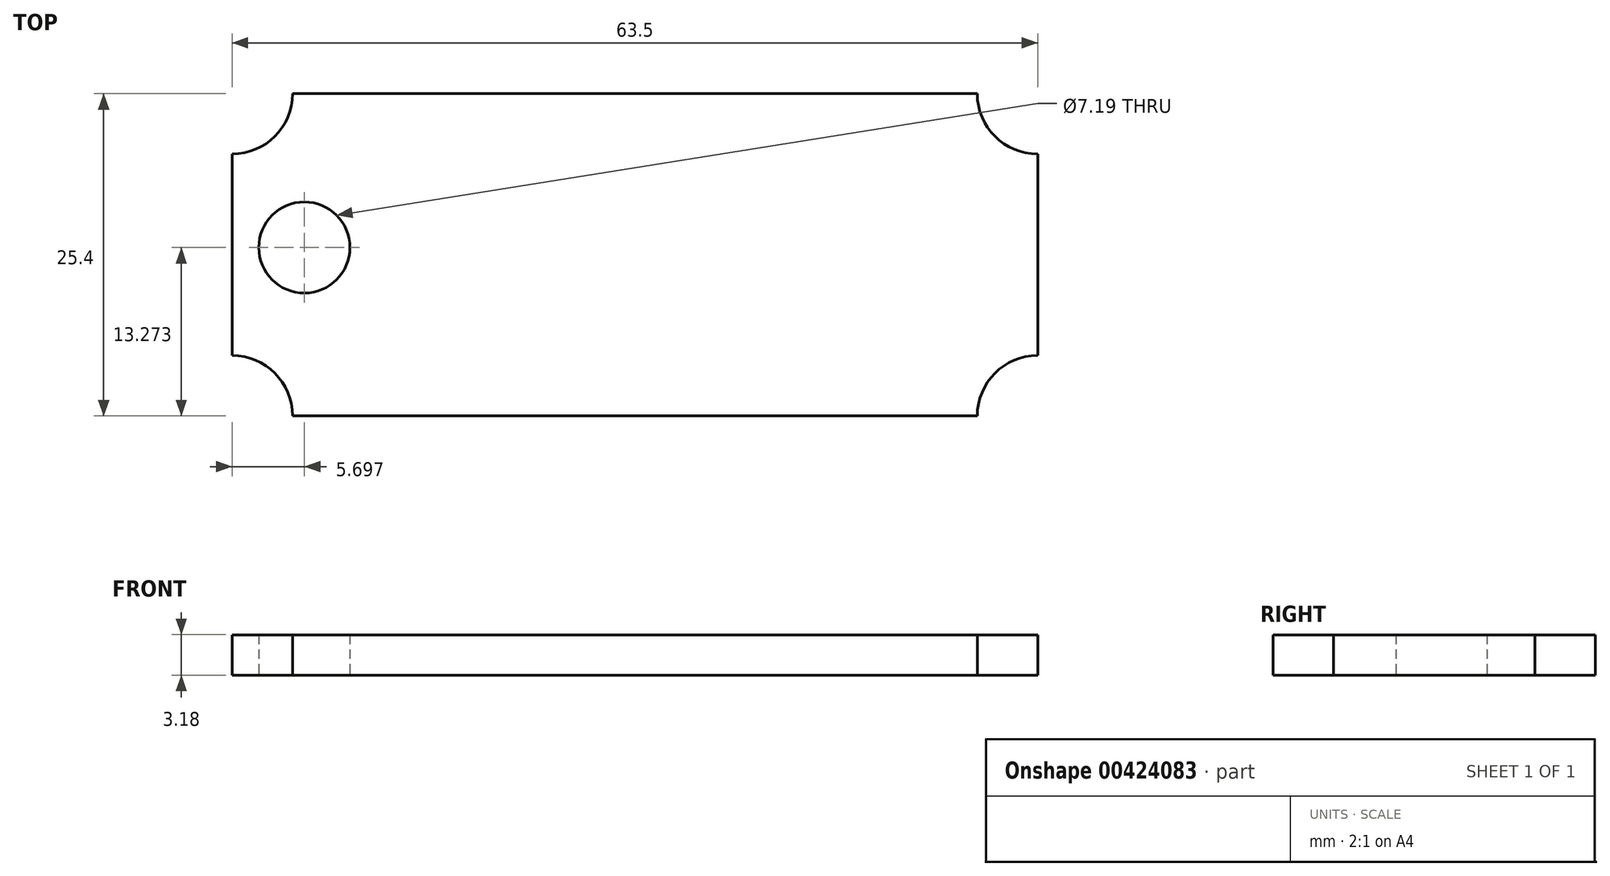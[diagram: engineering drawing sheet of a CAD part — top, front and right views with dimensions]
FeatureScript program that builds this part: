
annotation { "Feature Type Name" : "Feature", "Feature Type Description" : "" }
export const myFeature = defineFeature(function(context is Context, id is Id, definition is map)
    precondition{}
    {
        {
            var Q0;
            Q0=qCreatedBy(makeId("Top.planeOp"),FACE);
            var sketch = newSketch(context, id + "F0", { "sketchPlane" : qUnion([Q0])});
            skLineSegment(sketch, "E0.bottom", {"start": v(4.76, 0) * mm, "end": v(58.74, 0) * mm});
            skLineSegment(sketch, "E0.top", {"start": v(4.76, 25.4) * mm, "end": v(58.74, 25.4) * mm});
            skLineSegment(sketch, "E0.left", {"start": v(0, 4.76) * mm, "end": v(0, 20.64) * mm});
            skLineSegment(sketch, "E0.right", {"start": v(63.5, 4.76) * mm, "end": v(63.5, 20.64) * mm});
            skArc(sketch, "E1", {"start": v(0, 20.64) * mm, "mid": v(3.37, 22.03) * mm, "end": v(4.76, 25.4) * mm});
            skArc(sketch, "E2", {"start": v(4.76, 0) * mm, "mid": v(3.37, 3.37) * mm, "end": v(0, 4.76) * mm});
            skArc(sketch, "E3", {"start": v(58.74, 25.4) * mm, "mid": v(60.13, 22.03) * mm, "end": v(63.5, 20.64) * mm});
            skArc(sketch, "E4", {"start": v(63.5, 4.76) * mm, "mid": v(60.13, 3.37) * mm, "end": v(58.74, 0) * mm});
            skCircle(sketch, "E5", {"center": v(5.7, 13.27) * mm, "radius": 3.6 * mm});
            skSolve(sketch);
        }
        {
            var Q0;
            Q0=qSketchRegion(id+"F0",true);
            var Q1;
            Q1=makeQuery(id+"F0.imprint","IMPRINT",FACE,{"disambiguationData":[TD([[makeQuery(id+"F0.imprint","IMPRINT",EDGE,{"derivedFrom":sQuery(id+"F0.wireOp",EDGE,"E0.bottom")}),1.0]])]});
            extrude(context, id + "F1", {"entities" : qUnion([Q0, Q1]), "depth" : 3.17 * mm});
        }
    });
